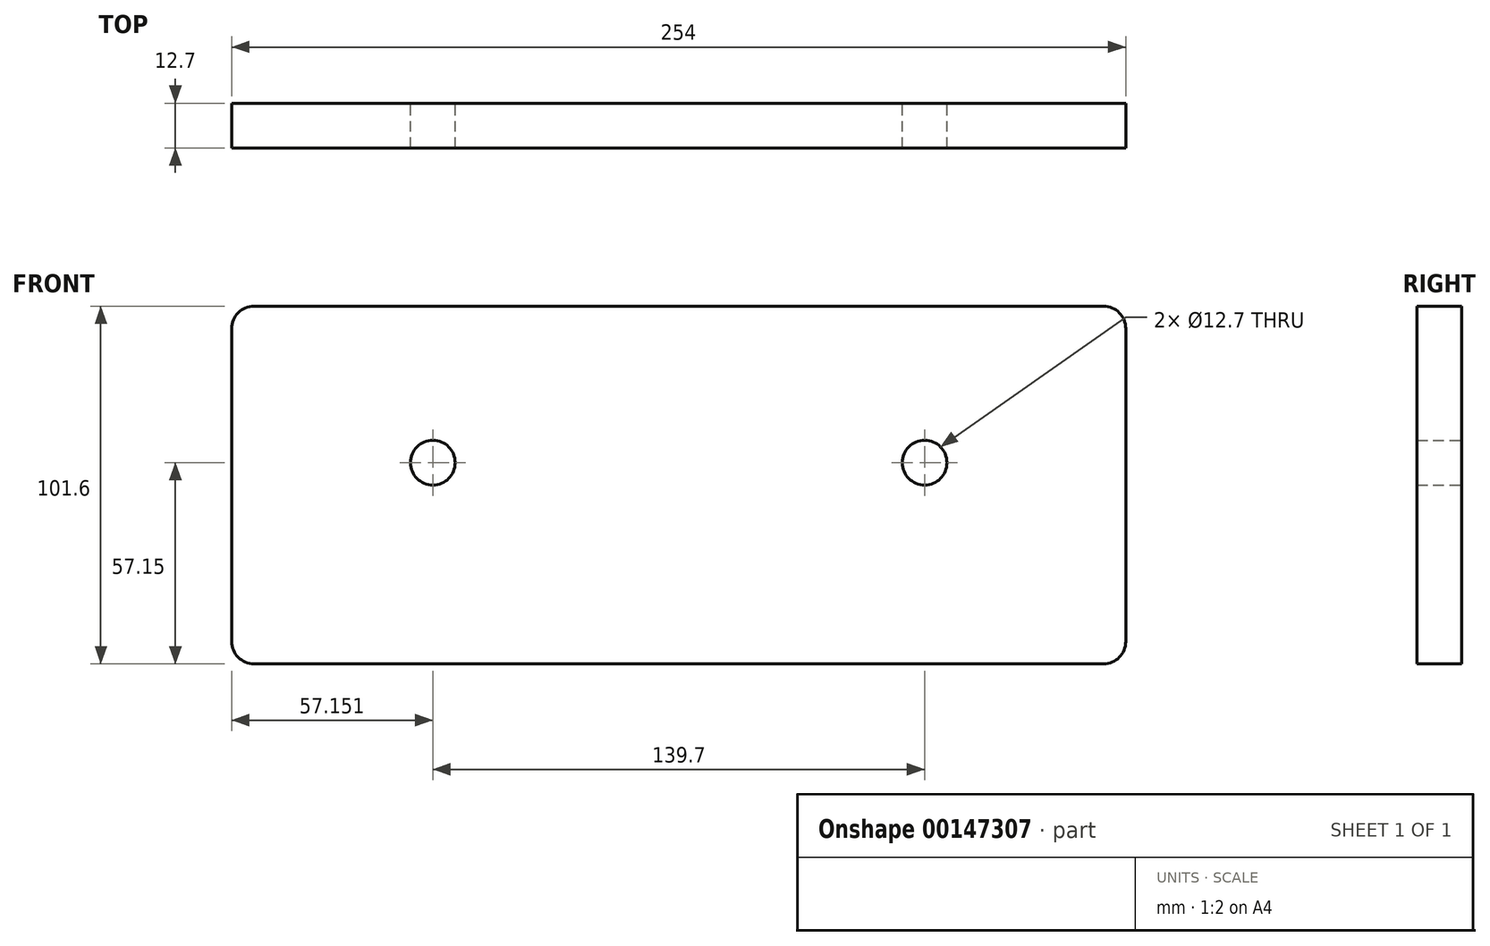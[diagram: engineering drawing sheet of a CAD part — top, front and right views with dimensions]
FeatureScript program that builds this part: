
annotation { "Feature Type Name" : "Feature", "Feature Type Description" : "" }
export const myFeature = defineFeature(function(context is Context, id is Id, definition is map)
    precondition{}
    {
        {
            var Q0;
            Q0=qCreatedBy(makeId("Front.planeOp"),FACE);
            var sketch = newSketch(context, id + "F0", { "sketchPlane" : qUnion([Q0])});
            skLineSegment(sketch, "E0.bottom", {"start": v(-127.46, 44.45) * mm, "end": v(126.54, 44.45) * mm});
            skLineSegment(sketch, "E0.top", {"start": v(-127.46, -57.15) * mm, "end": v(126.54, -57.15) * mm});
            skLineSegment(sketch, "E0.left", {"start": v(-127.46, 44.45) * mm, "end": v(-127.46, -57.15) * mm});
            skLineSegment(sketch, "E0.right", {"start": v(126.54, 44.45) * mm, "end": v(126.54, -57.15) * mm});
            skCircle(sketch, "E1", {"center": v(-70.3, 0) * mm, "radius": 6.35 * mm});
            skCircle(sketch, "E2", {"center": v(69.4, 0) * mm, "radius": 6.35 * mm});
            skSolve(sketch);
        }
        {
            var Q0;
            Q0=makeQuery(id+"F0.imprint","IMPRINT",FACE,{"disambiguationData":[TD([[makeQuery(id+"F0.imprint","IMPRINT",EDGE,{"derivedFrom":sQuery(id+"F0.wireOp",EDGE,"E0.bottom")}),-1.0]])]});
            extrude(context, id + "F1", {"entities" : qUnion([Q0]), "depth" : 12.7 * mm});
        }
        {
            var Q0;
            Q0=makeQuery(id+"F1.opExtrude","SWEPT_EDGE",EDGE,{"disambiguationData":[OSD([sQuery(id+"F0.wireOp",EDGE,"E0.bottom"),sQuery(id+"F0.wireOp",EDGE,"E0.left")])]});
            var Q1;
            Q1=makeQuery(id+"F1.opExtrude","SWEPT_EDGE",EDGE,{"disambiguationData":[OSD([sQuery(id+"F0.wireOp",EDGE,"E0.bottom"),sQuery(id+"F0.wireOp",EDGE,"E0.right")])]});
            var Q2;
            Q2=makeQuery(id+"F1.opExtrude","SWEPT_EDGE",EDGE,{"disambiguationData":[OSD([sQuery(id+"F0.wireOp",EDGE,"E0.top"),sQuery(id+"F0.wireOp",EDGE,"E0.left")])]});
            var Q3;
            Q3=makeQuery(id+"F1.opExtrude","SWEPT_EDGE",EDGE,{"disambiguationData":[OSD([sQuery(id+"F0.wireOp",EDGE,"E0.top"),sQuery(id+"F0.wireOp",EDGE,"E0.right")])]});
            fillet(context, id + "F2", {"entities" : qUnion([Q0, Q1, Q2, Q3]), "radius" : 6.35 * mm, "tangentPropagation" : true, "allowEdgeOverflow" : false});
        }
    });
